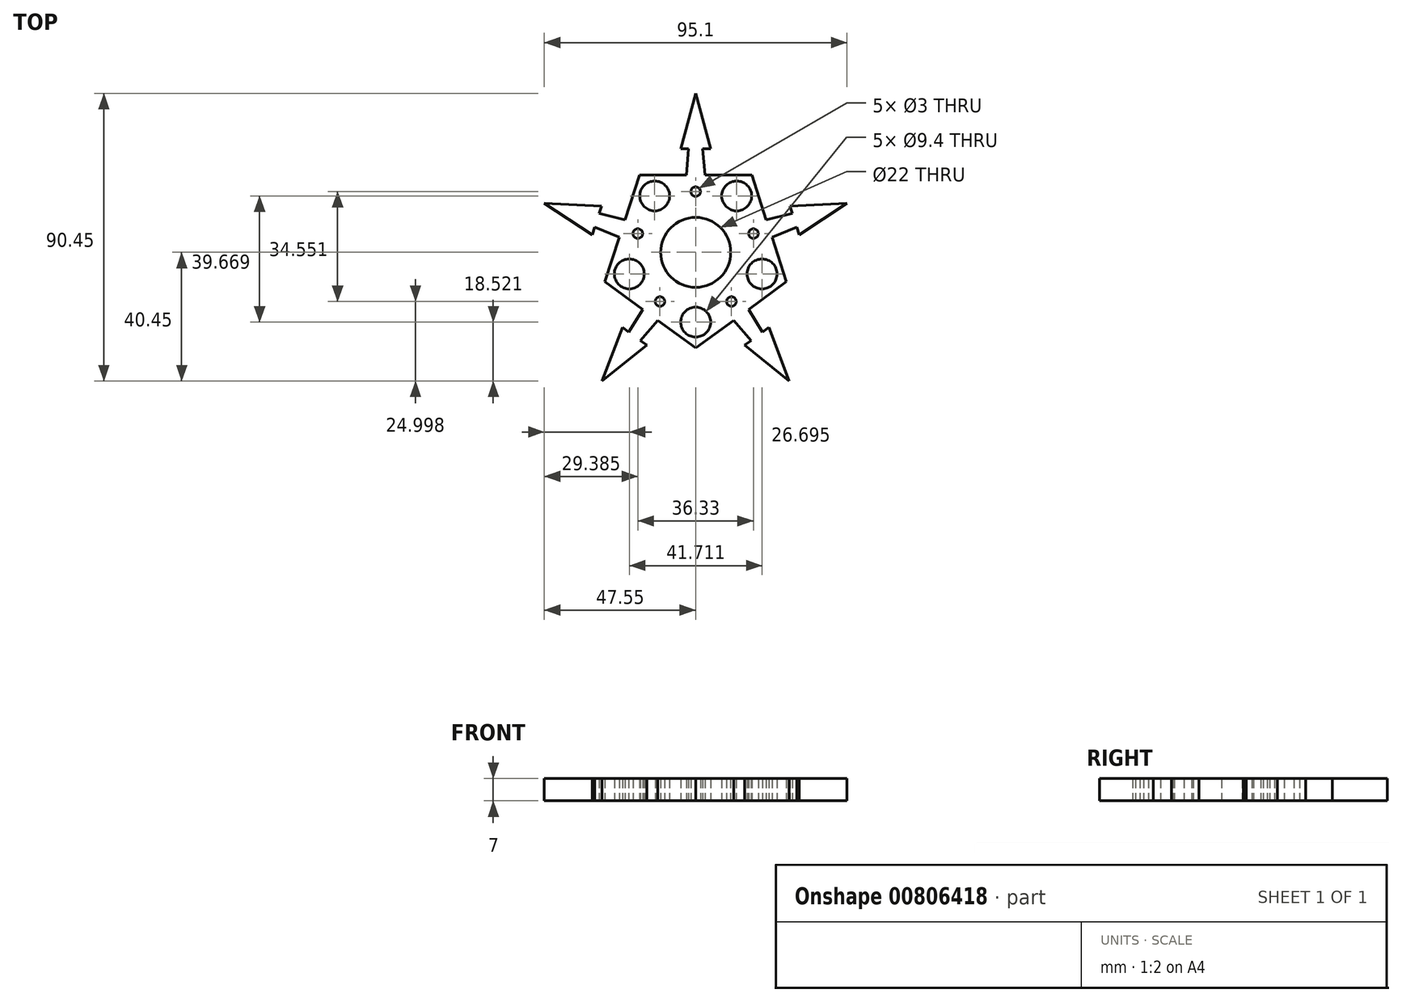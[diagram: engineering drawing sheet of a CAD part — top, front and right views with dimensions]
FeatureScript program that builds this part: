
annotation { "Feature Type Name" : "Feature", "Feature Type Description" : "" }
export const myFeature = defineFeature(function(context is Context, id is Id, definition is map)
    precondition{}
    {
        {
            var Q0;
            Q0=qCreatedBy(makeId("Top.planeOp"),FACE);
            var sketch = newSketch(context, id + "F0", { "sketchPlane" : qUnion([Q0])});
            skCircle(sketch, "E0", {"center": v(0, 0) * mm, "radius": 11 * mm});
            skLineSegment(sketch, "E1", {"start": v(0, 0) * mm, "end": v(0, 11) * mm});
            skLineSegment(sketch, "E2.0", {"start": v(0, -30) * mm, "end": v(-11.9, -21.35) * mm});
            skLineSegment(sketch, "E2.1", {"start": v(-28.53, -9.27) * mm, "end": v(-23.98, 4.72) * mm});
            skLineSegment(sketch, "E2.2", {"start": v(-17.63, 24.27) * mm, "end": v(-2.92, 24.27) * mm});
            skLineSegment(sketch, "E2.3", {"start": v(17.63, 24.27) * mm, "end": v(22.18, 10.28) * mm});
            skLineSegment(sketch, "E2.4", {"start": v(28.53, -9.27) * mm, "end": v(16.63, -17.92) * mm});
            skLineSegment(sketch, "E3", {"start": v(0, 50) * mm, "end": v(-4.74, 32.64) * mm});
            skLineSegment(sketch, "E4", {"start": v(-4.74, 32.64) * mm, "end": v(-2.24, 32.64) * mm});
            skLineSegment(sketch, "E5", {"start": v(-2.24, 32.64) * mm, "end": v(-2.92, 24.27) * mm});
            skLineSegment(sketch, "E6.MirrorCS", {"start": v(0, 50) * mm, "end": v(4.74, 32.64) * mm});
            skLineSegment(sketch, "E7.MirrorCS", {"start": v(4.74, 32.64) * mm, "end": v(2.24, 32.64) * mm});
            skLineSegment(sketch, "E8.MirrorCS", {"start": v(2.24, 32.64) * mm, "end": v(2.92, 24.27) * mm});
            skLineSegment(sketch, "E9.1.0", {"start": v(-47.55, 15.45) * mm, "end": v(-29.57, 14.6) * mm});
            skLineSegment(sketch, "E9.1.1", {"start": v(-47.55, 15.45) * mm, "end": v(-32.5, 5.58) * mm});
            skLineSegment(sketch, "E9.1.2", {"start": v(-32.5, 5.58) * mm, "end": v(-31.73, 7.95) * mm});
            skLineSegment(sketch, "E9.1.3", {"start": v(-31.73, 7.95) * mm, "end": v(-23.98, 4.72) * mm});
            skLineSegment(sketch, "E9.1.4", {"start": v(-30.35, 12.21) * mm, "end": v(-22.18, 10.28) * mm});
            skLineSegment(sketch, "E9.1.5", {"start": v(-29.57, 14.6) * mm, "end": v(-30.35, 12.21) * mm});
            skLineSegment(sketch, "E9.2.0", {"start": v(-29.39, -40.45) * mm, "end": v(-23.02, -23.62) * mm});
            skLineSegment(sketch, "E9.2.1", {"start": v(-29.39, -40.45) * mm, "end": v(-15.35, -29.19) * mm});
            skLineSegment(sketch, "E9.2.2", {"start": v(-15.35, -29.19) * mm, "end": v(-17.37, -27.72) * mm});
            skLineSegment(sketch, "E9.2.3", {"start": v(-17.37, -27.72) * mm, "end": v(-11.9, -21.35) * mm});
            skLineSegment(sketch, "E9.2.4", {"start": v(-21, -25.09) * mm, "end": v(-16.63, -17.92) * mm});
            skLineSegment(sketch, "E9.2.5", {"start": v(-23.02, -23.62) * mm, "end": v(-21, -25.09) * mm});
            skLineSegment(sketch, "E9.3.0", {"start": v(29.39, -40.45) * mm, "end": v(15.35, -29.19) * mm});
            skLineSegment(sketch, "E9.3.1", {"start": v(29.39, -40.45) * mm, "end": v(23.02, -23.62) * mm});
            skLineSegment(sketch, "E9.3.2", {"start": v(23.02, -23.62) * mm, "end": v(21, -25.09) * mm});
            skLineSegment(sketch, "E9.3.3", {"start": v(21, -25.09) * mm, "end": v(16.63, -17.92) * mm});
            skLineSegment(sketch, "E9.3.4", {"start": v(17.37, -27.72) * mm, "end": v(11.9, -21.35) * mm});
            skLineSegment(sketch, "E9.3.5", {"start": v(15.35, -29.19) * mm, "end": v(17.37, -27.72) * mm});
            skLineSegment(sketch, "E9.4.0", {"start": v(47.55, 15.45) * mm, "end": v(32.5, 5.58) * mm});
            skLineSegment(sketch, "E9.4.1", {"start": v(47.55, 15.45) * mm, "end": v(29.57, 14.6) * mm});
            skLineSegment(sketch, "E9.4.2", {"start": v(29.57, 14.6) * mm, "end": v(30.35, 12.21) * mm});
            skLineSegment(sketch, "E9.4.3", {"start": v(30.35, 12.21) * mm, "end": v(22.18, 10.28) * mm});
            skLineSegment(sketch, "E9.4.4", {"start": v(31.73, 7.95) * mm, "end": v(23.98, 4.72) * mm});
            skLineSegment(sketch, "E9.4.5", {"start": v(32.5, 5.58) * mm, "end": v(31.73, 7.95) * mm});
            skLineSegment(sketch, "E10.trimOffspring", {"start": v(-22.18, 10.28) * mm, "end": v(-17.63, 24.27) * mm});
            skLineSegment(sketch, "E11.trimOffspring", {"start": v(0, 24.27) * mm, "end": v(0, 50) * mm});
            skLineSegment(sketch, "E12.trimOffspring", {"start": v(2.92, 24.27) * mm, "end": v(17.63, 24.27) * mm});
            skLineSegment(sketch, "E13.trimOffspring", {"start": v(23.98, 4.72) * mm, "end": v(28.53, -9.27) * mm});
            skLineSegment(sketch, "E14.trimOffspring", {"start": v(11.9, -21.35) * mm, "end": v(0, -30) * mm});
            skLineSegment(sketch, "E15.trimOffspring", {"start": v(-16.63, -17.92) * mm, "end": v(-28.53, -9.27) * mm});
            skCircle(sketch, "E16", {"center": v(-12.89, 17.74) * mm, "radius": 4.7 * mm});
            skCircle(sketch, "E17.1.0", {"center": v(-20.86, -6.78) * mm, "radius": 4.7 * mm});
            skCircle(sketch, "E17.2.0", {"center": v(0, -21.93) * mm, "radius": 4.7 * mm});
            skCircle(sketch, "E17.3.0", {"center": v(20.86, -6.78) * mm, "radius": 4.7 * mm});
            skCircle(sketch, "E17.4.0", {"center": v(12.89, 17.74) * mm, "radius": 4.7 * mm});
            skCircle(sketch, "E18", {"center": v(0, 19.1) * mm, "radius": 1.5 * mm});
            skCircle(sketch, "E19.1.0", {"center": v(-18.16, 5.9) * mm, "radius": 1.5 * mm});
            skCircle(sketch, "E19.2.0", {"center": v(-11.23, -15.45) * mm, "radius": 1.5 * mm});
            skCircle(sketch, "E19.3.0", {"center": v(11.23, -15.45) * mm, "radius": 1.5 * mm});
            skCircle(sketch, "E19.4.0", {"center": v(18.16, 5.9) * mm, "radius": 1.5 * mm});
            skSolve(sketch);
        }
        {
            var Q0;
            Q0 = qSketchRegion(id + "F0", true);
            extrude(context, id + "F1", {"entities" : qUnion([Q0]), "depth" : 7 * mm, "offsetDistance" : 25 * mm});
        }
    });
